# Revit family: Беседка «Атмосфера» Арт 14663
name_source: partatom
category: Антураж
revit_build: Autodesk Revit 2018 (Build: 20180423_1000(x64)
units: mm (PartAtom-declared; Revit-internal decimal feet)

## family parameters
Всегда вертикально = Да
Источник визуального образа = Геометрия семейства
На основе рабочей плоскости = Нет
Общий = Нет
При загрузке вырезать с полостями = Нет
Точка расчета площади = Нет

## types (2) — shared parameters
URL = https://hobbyka.ru
Артикул товара = Арт. 14663
Группа модели = Навесы и беседки
Длина = 3580 мм
Изготовитель = ООО «Хоббика»
Материал изделия = Сталь, дерево, поликарбонат
Цвет каркаса = Сталь
Цвет отделки = Дерево
Цвет поликарбоната = Поликарбонат

## per-type parameters (varying)
| type | Без поликарбоната | Высота | Изображение типоразмера | С поликарбонатом | Ширина |
| Беседка «Атмосфера». Версия без поликарбоната | Да | 2700 мм | Беседка «Атмосфера» Арт 14663 без поликарбоната.jpg | Нет | 2020 мм |
| Беседка «Атмосфера». Версия с монолитным поликарбонатом | Нет | 2400 мм | Беседка «Атмосфера» Арт 14663 с монолитным поликарбонатом.jpg | Да | 2400 мм |

note: column(s) folded — value = type name in every type: Описание
